# Revit family: 1441xxx Edward Desk
name_source: partatom
category: Lighting Fixtures
units: mm (PartAtom-declared; Revit-internal decimal feet)

## family parameters
Always vertical = Yes
Cut with Voids When Loaded = No
Light Source = No
Maintain Annotation Orientation = No
OmniClass Number = 23.80.70.00
OmniClass Title = Lighting
Part Type = Normal
Room Calculation Point = No
Round Connector Dimension = Use Diameter
Shared = No
Work Plane-Based = No

## types (2) — shared parameters
Apparent Load = 0 VA
Manufacturer URL - Europe and Rest of World = www.astrolighting.com
Manufacturer URL - North America = us.astrolighting.com
zero-valued in all types: Default Elevation

## per-type parameters (varying)
| type | ADA compliant | Dimmable | Dimming Method | Driver Included | Driver Required | Efficacy (lm/W) | Electrical Class | Lamp | Length of Cable Supplied | Light Source Fixed | Location / IP Rating | Main Finish | Main Material | Power (W) | Product CCT | Product CRI | Product Dimensions (MM) | Product Location | Product Name | Product SKU | Product Weight (KG) |
| CE |  |  |  |  |  |  |  |  |  |  |  |  |  |  | 2700K / 3000K | 80/ 90 |  |  |  | 1234567 |  |
| ETL | Yes - if installed in compliance with ADA §307.2, 308, 309.3, 309.4 | No | Not Applicable | Not Applicable | No | Lamp Dependent (lm/W) | Not Applicable | LED | 2000 (mm) | No | Not Applicable | Matt Black | Metal Zinc | Lamp Dependent |  |  | 543 x 195 x 364 | Indoor | Edward Desk | 1441009 | 0.940 |

## geometry (parser evidence)
native form markers: Sweep x3
no freeform markers — native parametric forms only
